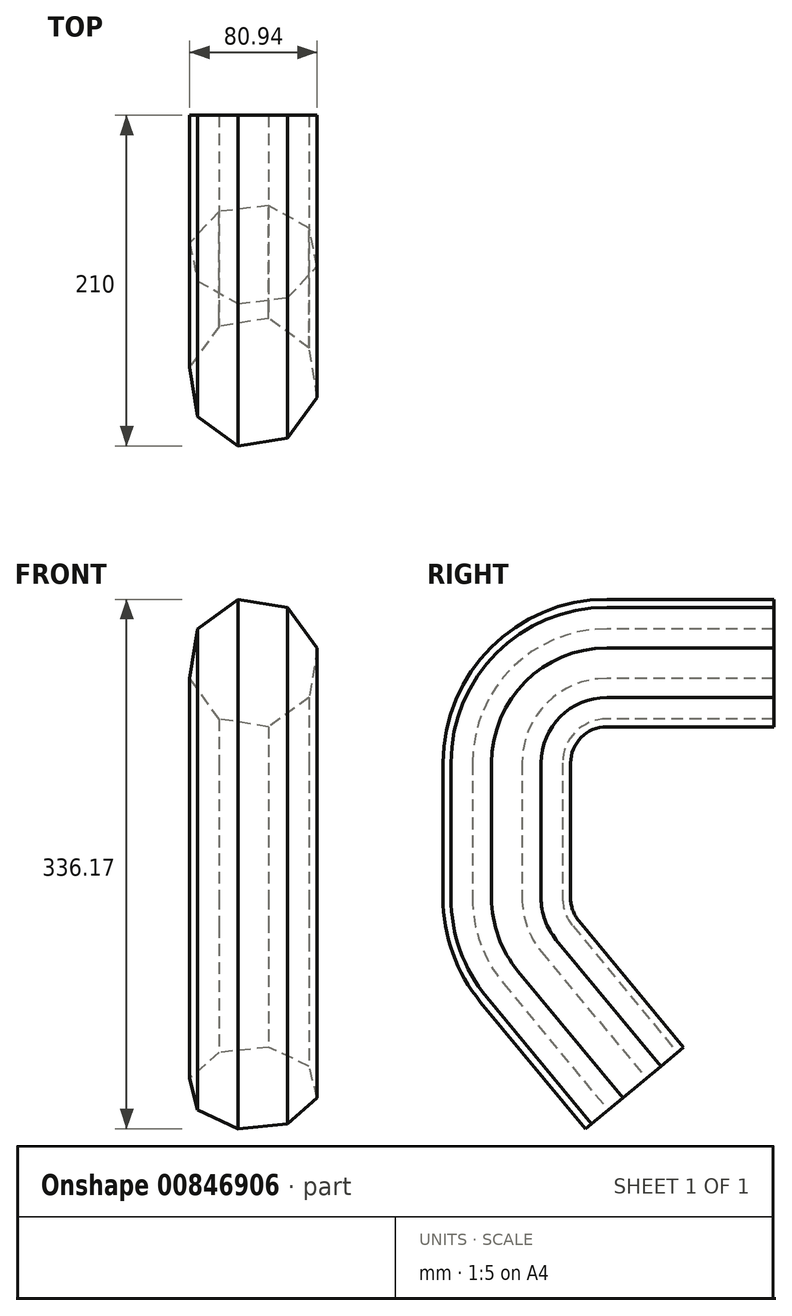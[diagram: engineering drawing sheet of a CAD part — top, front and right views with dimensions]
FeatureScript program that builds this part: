
annotation { "Feature Type Name" : "Feature", "Feature Type Description" : "" }
export const myFeature = defineFeature(function(context is Context, id is Id, definition is map)
    precondition{}
    {
        {
            var Q0;
            Q0=qCreatedBy(makeId("Front.planeOp"),FACE);
            var sketch = newSketch(context, id + "F0", { "sketchPlane" : qUnion([Q0])});
            skCircle(sketch, "E0.cCircle", {"center": v(0, 0) * mm, "radius": 38.44 * mm, "construction": true});
            skLineSegment(sketch, "E0.0", {"start": v(-40.47, -9.66) * mm, "end": v(-35.45, 21.79) * mm});
            skLineSegment(sketch, "E0.1", {"start": v(-35.45, 21.79) * mm, "end": v(-9.66, 40.47) * mm});
            skLineSegment(sketch, "E0.2", {"start": v(-9.66, 40.47) * mm, "end": v(21.79, 35.45) * mm});
            skLineSegment(sketch, "E0.3", {"start": v(21.79, 35.45) * mm, "end": v(40.47, 9.66) * mm});
            skLineSegment(sketch, "E0.4", {"start": v(40.47, 9.66) * mm, "end": v(35.45, -21.79) * mm});
            skLineSegment(sketch, "E0.5", {"start": v(35.45, -21.79) * mm, "end": v(9.66, -40.47) * mm});
            skLineSegment(sketch, "E0.6", {"start": v(9.66, -40.47) * mm, "end": v(-21.79, -35.45) * mm});
            skLineSegment(sketch, "E0.7", {"start": v(-21.79, -35.45) * mm, "end": v(-40.47, -9.66) * mm});
            skPoint(sketch, "E0.0.midPoint", {"position": v(-37.96, 6.06) * mm});
            skSolve(sketch);
        }
        {
            var Q0;
            Q0=qCreatedBy(makeId("Right.planeOp"),FACE);
            var sketch = newSketch(context, id + "F1", { "sketchPlane" : qUnion([Q0])});
            skLineSegment(sketch, "E1", {"start": v(0, 0) * mm, "end": v(-106.03, 0) * mm});
            skLineSegment(sketch, "E2", {"start": v(-169.53, -63.5) * mm, "end": v(-169.53, -149.08) * mm});
            skLineSegment(sketch, "E3", {"start": v(-154.95, -189.56) * mm, "end": v(-88.47, -269.9) * mm});
            skPoint(sketch, "E4.visualSharp", {"position": v(-169.53, 0) * mm});
            skArc(sketch, "E4.filletArc", {"start": v(-106.03, 0) * mm, "mid": v(-150.93, -18.6) * mm, "end": v(-169.53, -63.5) * mm});
            skPoint(sketch, "E5.visualSharp", {"position": v(-169.53, -171.95) * mm});
            skArc(sketch, "E5.filletArc", {"start": v(-169.53, -149.08) * mm, "mid": v(-165.77, -170.6) * mm, "end": v(-154.95, -189.56) * mm});
            skSolve(sketch);
        }
        {
            var Q0;
            Q0=makeQuery(id+"F0.imprint","IMPRINT",FACE,{"disambiguationData":[TD([[makeQuery(id+"F0.imprint","IMPRINT",EDGE,{"derivedFrom":sQuery(id+"F0.wireOp",EDGE,"E0.0")}),-1.0]])]});
            var Q1;
            Q1=sQuery(id+"F1.wireOp",EDGE,"E1");
            var Q2;
            Q2=sQuery(id+"F1.wireOp",EDGE,"E4.filletArc");
            var Q3;
            Q3=sQuery(id+"F1.wireOp",EDGE,"E2");
            var Q4;
            Q4=sQuery(id+"F1.wireOp",EDGE,"E5.filletArc");
            var Q5;
            Q5=sQuery(id+"F1.wireOp",EDGE,"E3");
            sweep(context, id + "F2", {"profiles" : qUnion([Q0]), "path" : qUnion([Q1, Q2, Q3, Q4, Q5])});
        }
    });
